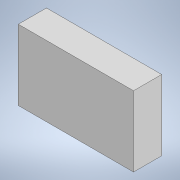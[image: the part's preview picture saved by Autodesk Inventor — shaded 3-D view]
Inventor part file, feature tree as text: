
AUTODESK INVENTOR PART (.ipt)
format: ipt  version: 2020 (Build 240168000, 168)  size: 85,504 bytes
history: native  units: mm
features: extrude x1, sketch x1
ambient origin geometry x8: Origin, YZ Plane, XZ Plane, XY Plane, X Axis, Y Axis, Z Axis, Center Point
bodies: Solide1 (feature_tree)
feature tree (2):
  extrude  "Extrusion1"  Depth=90.0mm
  sketch  "Esquisse1"
